# Revit family: 7060 Oslo 160 Silverxxxx
name_source: partatom
category: Lighting Fixtures
revit_build: Autodesk Revit LT 2014 (Build: 20130308_1515(x64)
units: mm (PartAtom-declared; Revit-internal decimal feet)

## types (2) — shared parameters
Apparent Load = 6 VA
Assembly Code = D5020200
Class = 1
Color Filter = 16777215
Description = Outdoor Light
Dimmable = No
Dimming Lamp Color Temperature Shift = <None>
Height = 160 mm  [stored 0.524934 ft]
IP Rating = IP65
Lamp = LED
Lamp included = Yes
Length = 100 mm  [stored 0.328084 ft]
Light Source From Wall = 72.5 mm  [stored 0.237861 ft]
Luminaire Lamp Efficiency Rating = A
Manufacturer = Astro Lighting Ltd, CM20 2DP
Mountable on normally flammable surfaces = Yes
Number of Poles = 1
Photometric Web File = 7060 OSLO 160.ies
Product Documentation = http://www.astrolighting.co.uk
Suitable for bathroom zone = Zones 1, 2 and 3
Tilt Angle = 0.00°
Type Comments = Includes integral LED driver.
URL = www.astrolighting.co.uk
Voltage = 230 V
Wattage Comments = 2 x 3w
Weight = 0.83kg
Width = 70 mm  [stored 0.229659 ft]

## per-type parameters (varying)
| type | Casing Material | Model |
| 7060 Oslo 160 (Silver) | Astro - Aluminium - Silver Paint | 7060 Oslo 160 Silver |
| 7061 Oslo 160 (Black) | Astro - Aluminium - Black Paint | 7061 Oslo 160 Black |

note: [stored X ft] marks values corroborated as IEEE doubles in the binary element streams (Revit-internal decimal feet)

## geometry (parser evidence)
native form markers: Sweep x2
no freeform markers — native parametric forms only
